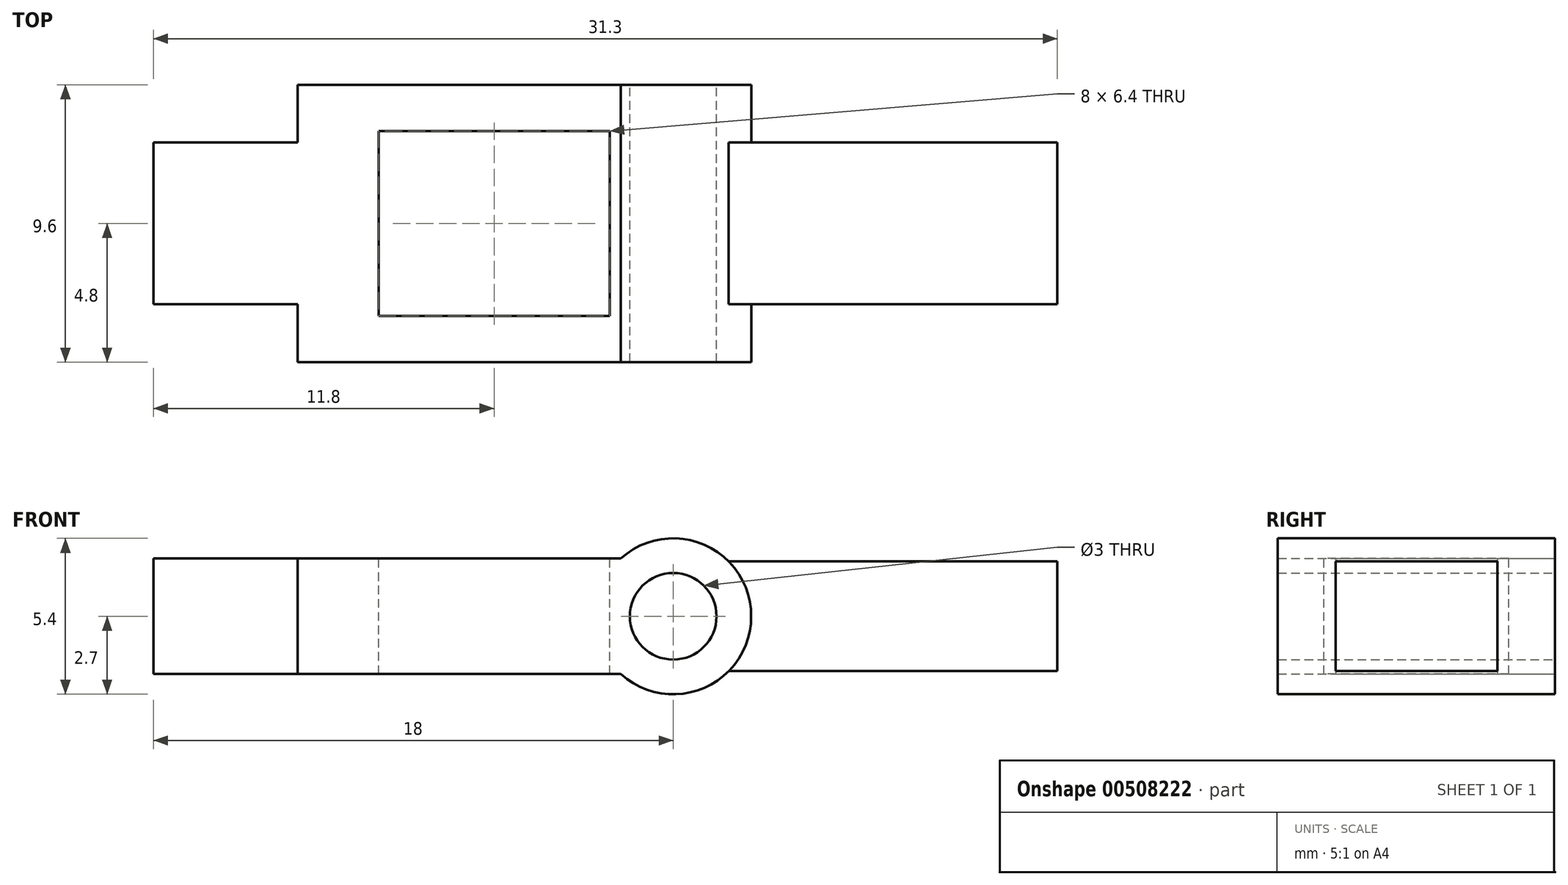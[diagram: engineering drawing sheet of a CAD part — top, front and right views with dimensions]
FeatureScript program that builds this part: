
annotation { "Feature Type Name" : "Feature", "Feature Type Description" : "" }
export const myFeature = defineFeature(function(context is Context, id is Id, definition is map)
    precondition{}
    {
        {
            var Q0;
            Q0=qCreatedBy(makeId("Front.planeOp"),FACE);
            var sketch = newSketch(context, id + "F0", { "sketchPlane" : qUnion([Q0])});
            skCircle(sketch, "E0", {"center": v(0, 0) * mm, "radius": 1.5 * mm});
            skArc(sketch, "E1", {"start": v(-1.81, -2) * mm, "mid": v(2.7, 0) * mm, "end": v(-1.81, 2) * mm});
            skLineSegment(sketch, "E2", {"start": v(-1.81, 2) * mm, "end": v(-13, 2) * mm});
            skLineSegment(sketch, "E3", {"start": v(-13, 2) * mm, "end": v(-13, -2) * mm});
            skLineSegment(sketch, "E4", {"start": v(-13, -2) * mm, "end": v(-1.81, -2) * mm});
            skLineSegment(sketch, "E5", {"start": v(1.92, 1.9) * mm, "end": v(13.3, 1.9) * mm});
            skLineSegment(sketch, "E6", {"start": v(13.3, 1.9) * mm, "end": v(13.3, -1.9) * mm});
            skLineSegment(sketch, "E7", {"start": v(13.3, -1.9) * mm, "end": v(1.92, -1.9) * mm});
            skLineSegment(sketch, "E8.bottom", {"start": v(-13, 2) * mm, "end": v(-18, 2) * mm});
            skLineSegment(sketch, "E8.top", {"start": v(-13, -2) * mm, "end": v(-18, -2) * mm});
            skLineSegment(sketch, "E8.right", {"start": v(-18, 2) * mm, "end": v(-18, -2) * mm});
            skSolve(sketch);
        }
        {
            var Q0;
            Q0=makeQuery(id+"F0.imprint","IMPRINT",FACE,{"disambiguationData":[TD([[makeQuery(id+"F0.imprint","IMPRINT",EDGE,{"derivedFrom":sQuery(id+"F0.wireOp",EDGE,"E0")}),-1.0]])]});
            extrude(context, id + "F1", {"entities" : qUnion([Q0]), "depth" : 9.6 * mm, "offsetDistance" : 25 * mm, "symmetric" : true});
        }
        {
            var Q0;
            {var subQ0=sQuery(id+"F0.wireOp",EDGE,"E5");Q0=makeQuery(id+"F0.imprint","IMPRINT",FACE,{"disambiguationData":[TD([[makeQuery(id+"F0.imprint","IMPRINT",EDGE,{"derivedFrom":subQ0}),-1.0]])]});}
            var Q1;
            Q1=makeQuery(id+"F0.imprint","IMPRINT",FACE,{"disambiguationData":[TD([[makeQuery(id+"F0.imprint","IMPRINT",EDGE,{"derivedFrom":sQuery(id+"F0.wireOp",EDGE,"E3")}),-1.0]])]});
            extrude(context, id + "F2", {"entities" : qUnion([Q0, Q1]), "operationType" : NewBodyOperationType.ADD, "depth" : 5.6 * mm, "offsetDistance" : 25 * mm, "symmetric" : true});
        }
        {
            var Q0;
            Q0=makeQuery(id+"F2.boolean.opBoolean","MERGE",FACE,{"derivedFrom":[makeQuery(id+"F1.opExtrude","SWEPT_FACE",FACE,{"disambiguationData":[OSD([sQuery(id+"F0.wireOp",EDGE,"E2")])]}),makeQuery(id+"F2.opExtrude","SWEPT_FACE",FACE,{"disambiguationData":[OSD([sQuery(id+"F0.wireOp",EDGE,"E8.bottom")])]})]});
            var sketch = newSketch(context, id + "F3", { "sketchPlane" : qUnion([Q0])});
            skLineSegment(sketch, "E9.bottom", {"start": v(-10.2, 3.2) * mm, "end": v(-2.2, 3.2) * mm});
            skLineSegment(sketch, "E9.top", {"start": v(-10.2, -3.2) * mm, "end": v(-2.2, -3.2) * mm});
            skLineSegment(sketch, "E9.left", {"start": v(-10.2, 3.2) * mm, "end": v(-10.2, -3.2) * mm});
            skLineSegment(sketch, "E9.right", {"start": v(-2.2, 3.2) * mm, "end": v(-2.2, -3.2) * mm});
            skLineSegment(sketch, "E10", {"start": v(0, 0) * mm, "end": v(-2.2, 0) * mm, "construction": true});
            skSolve(sketch);
        }
        {
            var Q0;
            Q0 = qSketchRegion(id + "F3", true);
            extrude(context, id + "F4", {"entities" : qUnion([Q0]), "operationType" : NewBodyOperationType.REMOVE, "endBound" : BoundingType.THROUGH_ALL, "oppositeDirection" : true, "depth" : 25 * mm, "offsetDistance" : 25 * mm});
        }
    });
